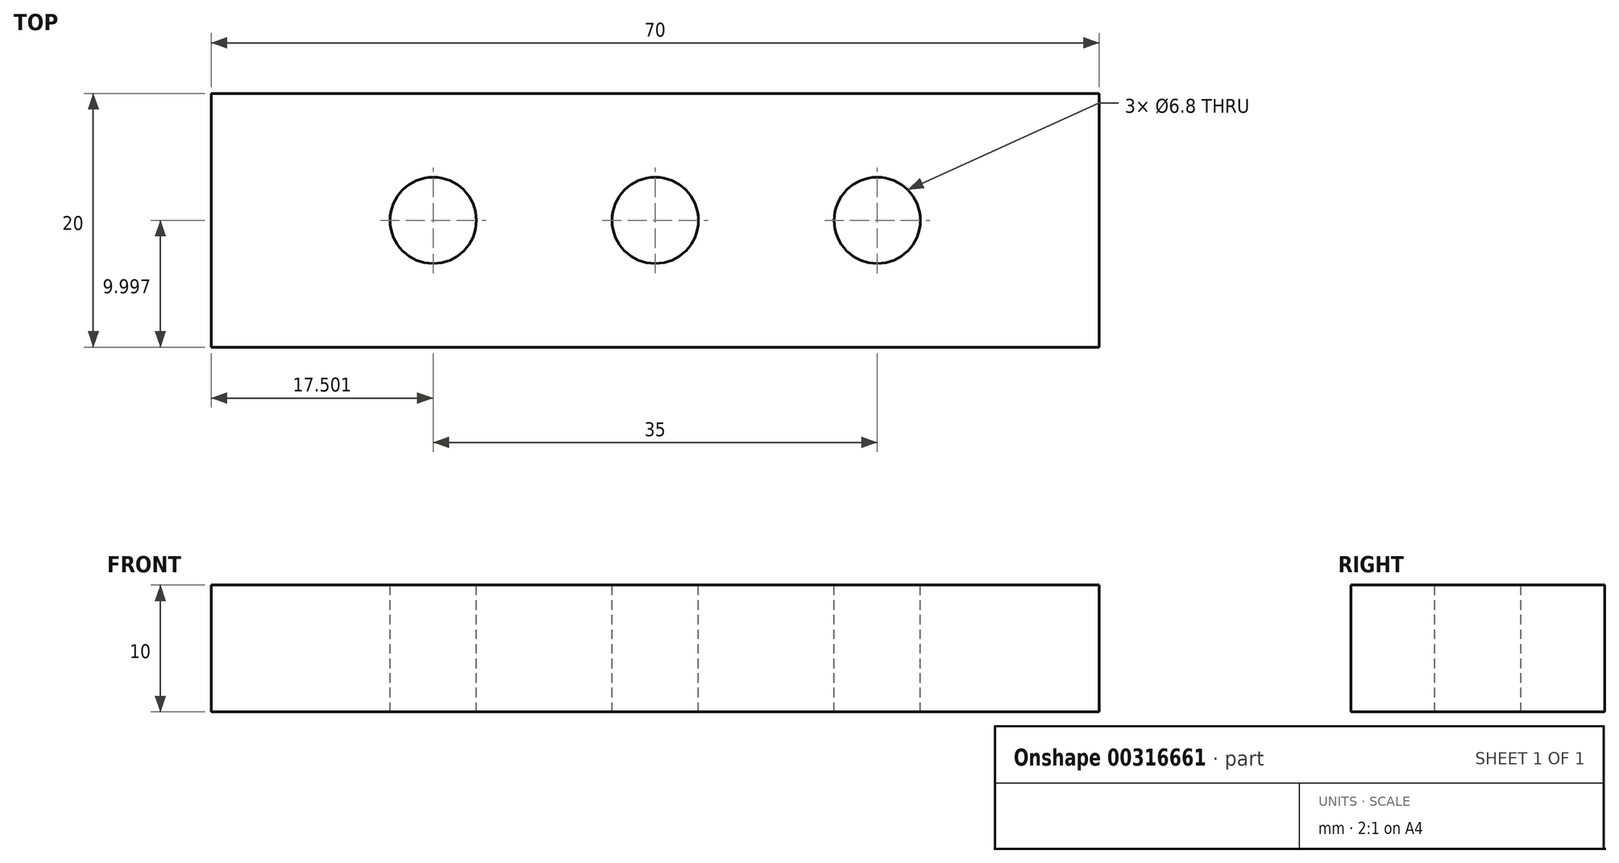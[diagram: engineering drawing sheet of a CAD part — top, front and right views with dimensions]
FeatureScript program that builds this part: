
annotation { "Feature Type Name" : "Feature", "Feature Type Description" : "" }
export const myFeature = defineFeature(function(context is Context, id is Id, definition is map)
    precondition{}
    {
        {
            var Q0;
            Q0=qCreatedBy(makeId("Top.planeOp"),FACE);
            var sketch = newSketch(context, id + "F0", { "sketchPlane" : qUnion([Q0])});
            skLineSegment(sketch, "E0.bottom", {"start": v(-25.39, 8.72) * mm, "end": v(44.61, 8.72) * mm});
            skLineSegment(sketch, "E0.top", {"start": v(-25.39, -11.28) * mm, "end": v(44.61, -11.28) * mm});
            skLineSegment(sketch, "E0.left", {"start": v(-25.39, 8.72) * mm, "end": v(-25.39, -11.28) * mm});
            skLineSegment(sketch, "E0.right", {"start": v(44.61, 8.72) * mm, "end": v(44.61, -11.28) * mm});
            skSolve(sketch);
        }
        {
            var Q0;
            Q0 = qSketchRegion(id + "F0", true);
            extrude(context, id + "F1", {"entities" : qUnion([Q0]), "depth" : 10 * mm});
        }
        {
            var Q0;
            Q0=makeQuery(id+"F1.opExtrude","CAP_FACE",FACE,{"disambiguationData":[OSD([sQuery(id+"F0.wireOp",EDGE,"E0.bottom"),sQuery(id+"F0.wireOp",EDGE,"E0.top"),sQuery(id+"F0.wireOp",EDGE,"E0.left"),sQuery(id+"F0.wireOp",EDGE,"E0.right")])],"isStart":false});
            var sketch = newSketch(context, id + "F2", { "sketchPlane" : qUnion([Q0])});
            skPoint(sketch, "E1", {"position": v(9.61, -1.28) * mm});
            skPoint(sketch, "E1.positionSnap0", {"position": v(9.61, 8.72) * mm});
            skPoint(sketch, "E1.positionSnap1", {"position": v(-25.39, -1.28) * mm});
            skPoint(sketch, "E2", {"position": v(-7.89, -1.28) * mm});
            skPoint(sketch, "E3", {"position": v(27.11, -1.28) * mm});
            skSolve(sketch);
        }
        {
            var Q0;
            Q0=sQuery(id+"F2.wireOp",VERTEX,"E3");
            var Q1;
            Q1=sQuery(id+"F2.wireOp",VERTEX,"E1");
            var Q2;
            Q2=sQuery(id+"F2.wireOp",VERTEX,"E2");
            var Q3;
            Q3=makeQuery(id+"F1.opExtrude","SWEPT_BODY",BODY,{"disambiguationData":[OSD([sQuery(id+"F0.wireOp",EDGE,"E0.bottom"),sQuery(id+"F0.wireOp",EDGE,"E0.top"),sQuery(id+"F0.wireOp",EDGE,"E0.left"),sQuery(id+"F0.wireOp",EDGE,"E0.right")])]});
            hole(context, id + "F3", {"style" : HoleStyle.SIMPLE, "endStyle" : HoleEndStyle.BLIND, "standardTappedOrClearance" : lookupTablePath({ "standard" : "ISO", "engagement" : "75%", "pitch" : "1.25 mm", "size" : "M8", "type" : "Tapped" }), "standardBlindInLast" : lookupTablePath({ "standard" : "ISO", "engagement" : "75%", "pitch" : "1.25 mm", "size" : "M8", "type" : "Tapped" }), "holeDiameter" : 6.8 * mm, "showTappedDepth" : true, "holeDepth" : 15.75 * mm, "isTappedThrough" : true, "tappedDepth" : 12 * mm, "tapClearance" : 3, "startFromSketch" : true, "locations" : qUnion([Q0, Q1, Q2]), "scope" : qUnion([Q3]), "majorDiameter" : 8 * mm});
        }
    });
